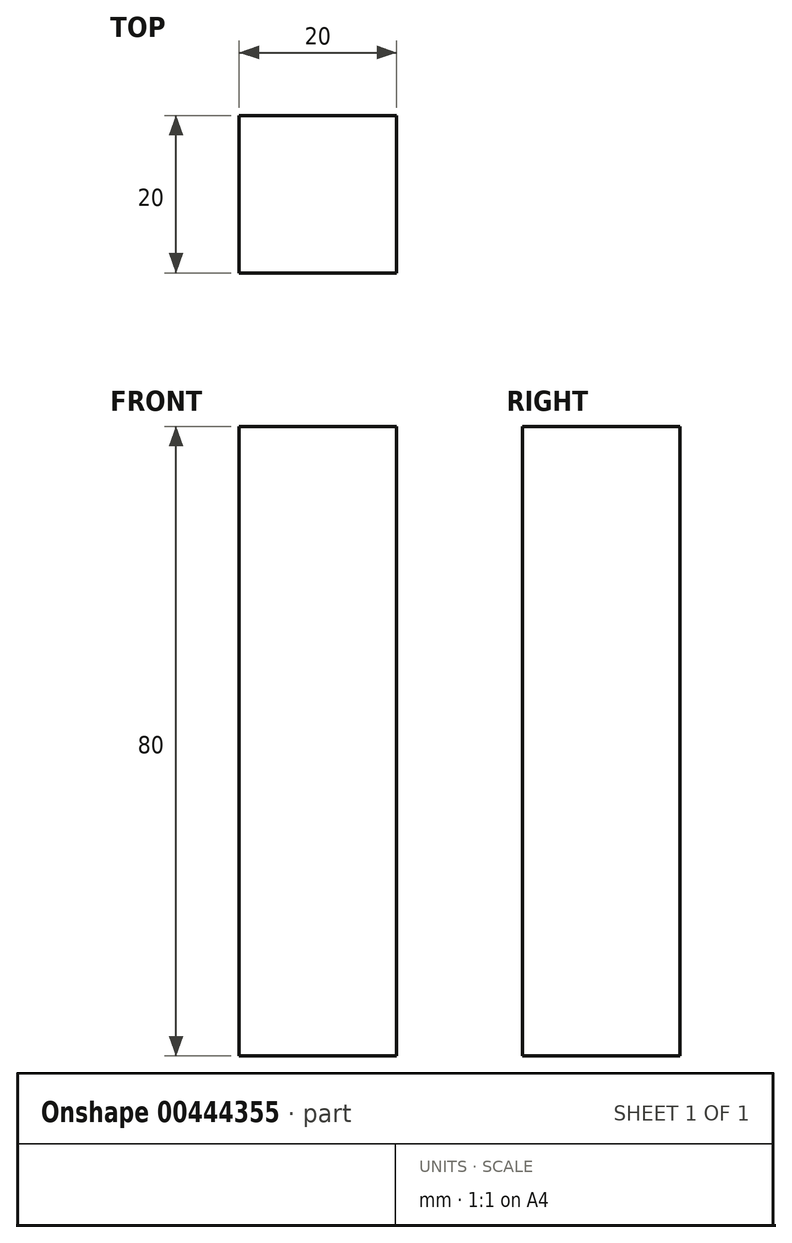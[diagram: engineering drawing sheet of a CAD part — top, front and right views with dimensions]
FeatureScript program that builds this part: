
annotation { "Feature Type Name" : "Feature", "Feature Type Description" : "" }
export const myFeature = defineFeature(function(context is Context, id is Id, definition is map)
    precondition{}
    {
        {
            var Q0;
            Q0=qCreatedBy(makeId("Top.planeOp"),FACE);
            var sketch = newSketch(context, id + "F0", { "sketchPlane" : qUnion([Q0])});
            skLineSegment(sketch, "E0.bottom", {"start": v(10, -10) * mm, "end": v(-10, -10) * mm});
            skLineSegment(sketch, "E0.top", {"start": v(10, 10) * mm, "end": v(-10, 10) * mm});
            skLineSegment(sketch, "E0.left", {"start": v(10, -10) * mm, "end": v(10, 10) * mm});
            skLineSegment(sketch, "E0.right", {"start": v(-10, -10) * mm, "end": v(-10, 10) * mm});
            skPoint(sketch, "E0.middle", {"position": v(0, 0) * mm});
            skSolve(sketch);
        }
        {
            var Q0;
            Q0 = qSketchRegion(id + "F0", true);
            extrude(context, id + "F1", {"entities" : qUnion([Q0]), "flatOperationType" : FlatOperationType.REMOVE, "offsetDistance" : 25 * mm, "depth" : 80 * mm, "domain" : OperationDomain.MODEL});
        }
    });
